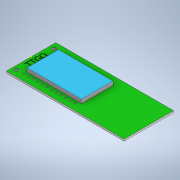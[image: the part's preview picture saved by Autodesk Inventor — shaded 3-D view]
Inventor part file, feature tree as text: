
AUTODESK INVENTOR PART (.ipt)
format: ipt  version: 2020 (Build 240168000, 168)  size: 205,824 bytes
history: native  units: mm
features: other x28, sketch x7, extrude x3, plane x3, hole x2, projected_geometry x1
ambient origin geometry x8: Origin, YZ Plane, XZ Plane, XY Plane, X Axis, Y Axis, Z Axis, Center Point
bodies: Body1 (feature_tree)
feature tree (44):
  other  "Sólido1"
  extrude  "Extrusión1"  Depth=27.0mm
  hole  "Agujero1"  [1 undecoded]
  hole  "Agujero2"  [1 undecoded]
  other  "Eje de trabajo1"
  other  "Eje de trabajo2"
  other  "Eje de trabajo3"
  other  "Eje de trabajo4"
  other  "Eje de trabajo5"
  other  "Eje de trabajo6"
  other  "Eje de trabajo7"
  other  "Eje de trabajo8"
  other  "Eje de trabajo9"
  other  "Eje de trabajo10"
  other  "Eje de trabajo11"
  other  "Eje de trabajo12"
  other  "Eje de trabajo13"
  other  "Eje de trabajo14"
  other  "Eje de trabajo15"
  other  "Eje de trabajo16"
  other  "Eje de trabajo17"
  other  "Eje de trabajo18"
  other  "Eje de trabajo19"
  other  "Eje de trabajo20"
  other  "Eje de trabajo21"
  other  "Eje de trabajo22"
  other  "Eje de trabajo23"
  other  "Eje de trabajo24"
  sketch  "Boceto4"  dims[d8=2.54mm d9=2.54mm]
  plane  "Plano de trabajo1"
  plane  "Plano de trabajo5"
  other  "Eje de trabajo25"
  other  "Eje de trabajo26"
  extrude  "Extrusión2"  Depth=2.54mm
  sketch  "Boceto6"  dims[d12=2.54mm]
  extrude  "Extrusión3"  Depth=2.54mm
  other  "antena"
  sketch  "Boceto1"  dims[d0=1.0mm d1=27.0mm]
  sketch  "Boceto2"  dims[d2=13.5mm d3=64.47mm d4=0.0mm]
  projected_geometry  "Contorno proyectado1"
  sketch  "Boceto3"  dims[d5=3.44mm d6=2.56mm]
  plane  "Plano de trabajo6"
  sketch  "Boceto5"  dims[d10=2.54mm d11=2.54mm]
  sketch  "Boceto7"  dims[d13=2.54mm d14=2.54mm d15=2.54mm d16=2.54mm d17=2.54mm d18=2.54mm d19=3.54mm d21=0.9mm d22=6.0mm d23=4.0mm d24=2.0mm d25=90.0deg d26=8.0mm d27=20.594885mm d28=2.0mm d29=6.0mm d30=4.0mm d31=2.0mm d32=90.0deg d33=8.0mm d34=20.594885mm d35=0.0mm d39=-2.317mm d40=-2.317mm d41=2.0mm d42=0.0mm d43=13.5mm d44=2.0mm d45=1.0mm d46=1.0mm d47=0.5mm d48=0.5mm d49=0.2mm d50=0.0mm]
note: 2 required parameter values undecoded (feature->parameter linkage not recoverable at this tier; creation-order binding heuristic only, values carry confidence <= 0.55)
